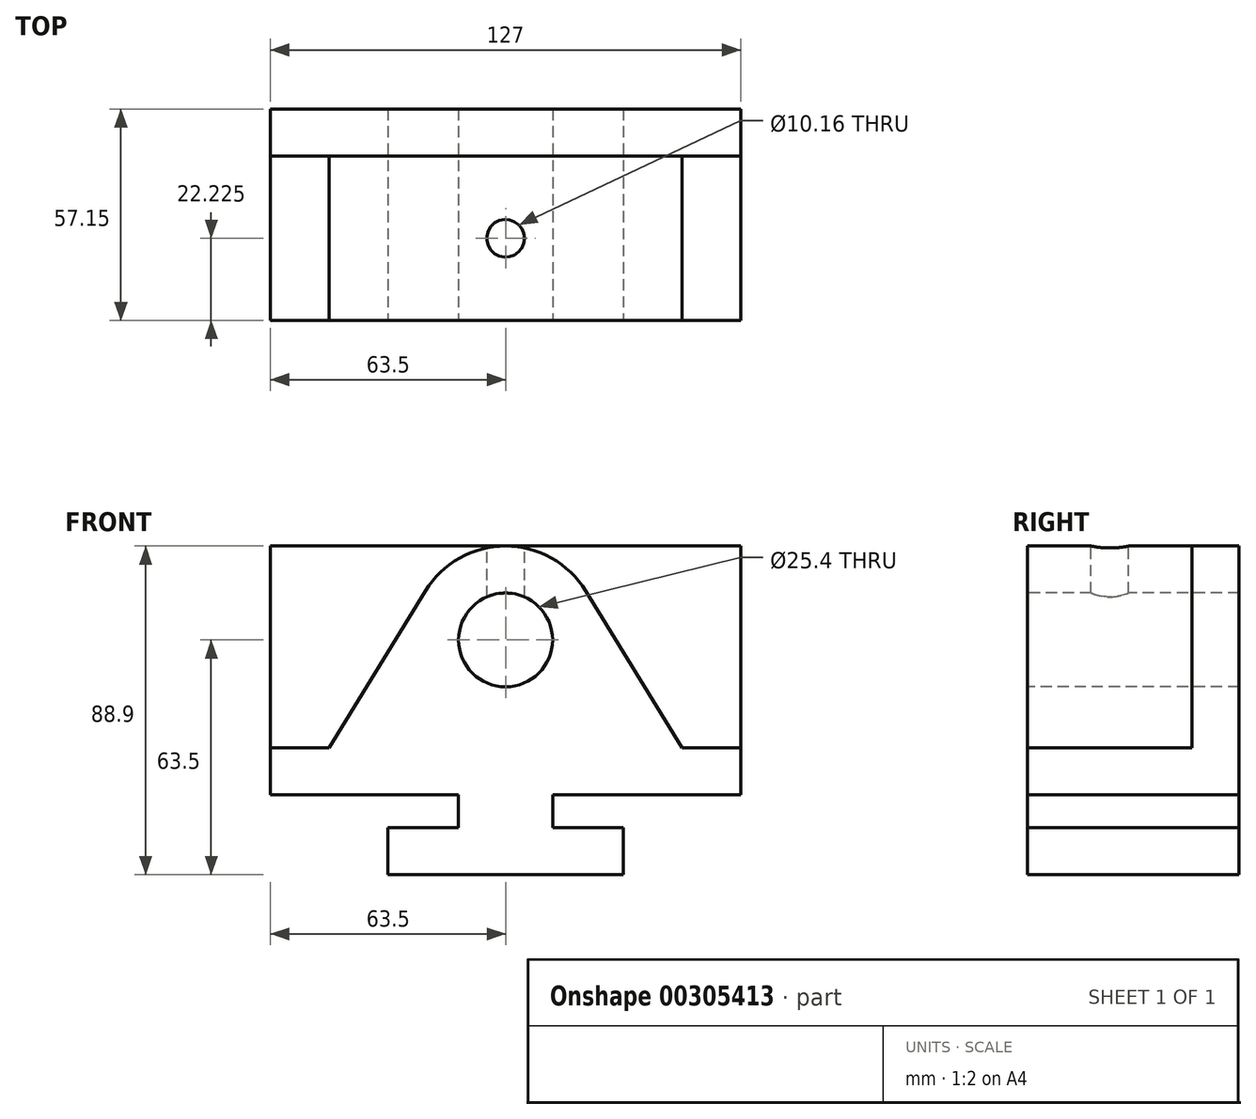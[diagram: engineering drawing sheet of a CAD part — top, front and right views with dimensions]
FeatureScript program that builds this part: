
annotation { "Feature Type Name" : "Feature", "Feature Type Description" : "" }
export const myFeature = defineFeature(function(context is Context, id is Id, definition is map)
    precondition{}
    {
        {
            var Q0;
            Q0=qCreatedBy(makeId("Front.planeOp"),FACE);
            var sketch = newSketch(context, id + "F0", { "sketchPlane" : qUnion([Q0])});
            skLineSegment(sketch, "E0.bottom", {"start": v(0, 0) * mm, "end": v(127, 0) * mm});
            skLineSegment(sketch, "E0.top", {"start": v(0, 88.9) * mm, "end": v(127, 88.9) * mm});
            skLineSegment(sketch, "E0.left", {"start": v(0, 0) * mm, "end": v(0, 88.9) * mm});
            skLineSegment(sketch, "E0.right", {"start": v(127, 0) * mm, "end": v(127, 88.9) * mm});
            skSolve(sketch);
        }
        {
            var Q0;
            Q0 = qSketchRegion(id + "F0", true);
            extrude(context, id + "F1", {"entities" : qUnion([Q0]), "depth" : 57.15 * mm});
        }
        {
            var Q0;
            Q0=makeQuery(id+"F1.opExtrude","CAP_FACE",FACE,{"disambiguationData":[OSD([sQuery(id+"F0.wireOp",EDGE,"E0.bottom"),sQuery(id+"F0.wireOp",EDGE,"E0.top"),sQuery(id+"F0.wireOp",EDGE,"E0.left"),sQuery(id+"F0.wireOp",EDGE,"E0.right")])],"isStart":false});
            var sketch = newSketch(context, id + "F2", { "sketchPlane" : qUnion([Q0])});
            skCircle(sketch, "E1", {"center": v(63.5, 63.5) * mm, "radius": 12.7 * mm});
            skArc(sketch, "E2", {"start": v(85.17, 76.75) * mm, "mid": v(63.5, 88.9) * mm, "end": v(41.83, 76.75) * mm});
            skLineSegment(sketch, "E3", {"start": v(0, 34.3) * mm, "end": v(15.88, 34.3) * mm});
            skLineSegment(sketch, "E4", {"start": v(15.88, 34.3) * mm, "end": v(41.83, 76.75) * mm});
            skLineSegment(sketch, "E5", {"start": v(127, 34.3) * mm, "end": v(111.12, 34.3) * mm});
            skLineSegment(sketch, "E6", {"start": v(111.12, 34.3) * mm, "end": v(85.17, 76.75) * mm});
            skLineSegment(sketch, "E7", {"start": v(0, 21.59) * mm, "end": v(50.8, 21.59) * mm});
            skLineSegment(sketch, "E8", {"start": v(50.8, 21.59) * mm, "end": v(50.8, 12.7) * mm});
            skLineSegment(sketch, "E9", {"start": v(76.2, 21.6) * mm, "end": v(76.2, 12.7) * mm});
            skLineSegment(sketch, "E10.trimOffspring", {"start": v(76.2, 21.59) * mm, "end": v(127, 21.59) * mm});
            skLineSegment(sketch, "E11", {"start": v(76.2, 12.7) * mm, "end": v(95.25, 12.7) * mm});
            skLineSegment(sketch, "E12", {"start": v(50.8, 12.7) * mm, "end": v(31.75, 12.7) * mm});
            skLineSegment(sketch, "E13", {"start": v(31.75, 12.7) * mm, "end": v(31.75, 0) * mm});
            skLineSegment(sketch, "E14", {"start": v(31.75, 0) * mm, "end": v(95.25, 0) * mm});
            skLineSegment(sketch, "E15", {"start": v(95.25, 0) * mm, "end": v(95.25, 12.7) * mm});
            skSolve(sketch);
        }
        {
            var Q0;
            Q0 = qSketchRegion(id + "F2", true);
            var Q1;
            Q1=makeQuery(id+"F2.imprint","IMPRINT",FACE,{"disambiguationData":[TD([[makeQuery(id+"F2.imprint","IMPRINT",EDGE,{"derivedFrom":sQuery(id+"F2.wireOp",EDGE,"E9")}),1.0]])]});
            var Q2;
            {var subQ1=sQuery(id+"F2.wireOp",EDGE,"E7");Q2=makeQuery(id+"F2.imprint","IMPRINT",FACE,{"disambiguationData":[TD([[makeQuery(id+"F2.imprint","IMPRINT",EDGE,{"derivedFrom":subQ1}),-1.0]])]});}
            extrude(context, id + "F3", {"entities" : qUnion([Q0, Q1, Q2]), "operationType" : NewBodyOperationType.REMOVE, "endBound" : BoundingType.THROUGH_ALL, "oppositeDirection" : true, "depth" : 25.4 * mm});
        }
        {
            var Q0;
            Q0=makeQuery(id+"F1.opExtrude","CAP_FACE",FACE,{"disambiguationData":[OSD([sQuery(id+"F0.wireOp",EDGE,"E0.bottom"),sQuery(id+"F0.wireOp",EDGE,"E0.top"),sQuery(id+"F0.wireOp",EDGE,"E0.left"),sQuery(id+"F0.wireOp",EDGE,"E0.right")])],"isStart":false});
            var sketch = newSketch(context, id + "F4", { "sketchPlane" : qUnion([Q0])});
            skCircle(sketch, "E16", {"center": v(63.5, 63.5) * mm, "radius": 25.4 * mm});
            skLineSegment(sketch, "E17", {"start": v(0, 34.3) * mm, "end": v(15.88, 34.3) * mm});
            skLineSegment(sketch, "E18", {"start": v(127, 34.3) * mm, "end": v(111.12, 34.3) * mm});
            skLineSegment(sketch, "E19", {"start": v(15.88, 34.3) * mm, "end": v(41.83, 76.75) * mm});
            skLineSegment(sketch, "E20", {"start": v(111.12, 34.3) * mm, "end": v(85.17, 76.75) * mm});
            skSolve(sketch);
        }
        {
            var Q0;
            {var subQ6=sQuery(id+"F4.wireOp",EDGE,"E17");Q0=makeQuery(id+"F4.imprint","IMPRINT",FACE,{"disambiguationData":[TD([[makeQuery(id+"F4.imprint","IMPRINT",EDGE,{"derivedFrom":subQ6}),1.0]])]});}
            var Q1;
            {var subQ6=sQuery(id+"F4.wireOp",EDGE,"E18");Q1=makeQuery(id+"F4.imprint","IMPRINT",FACE,{"disambiguationData":[TD([[makeQuery(id+"F4.imprint","IMPRINT",EDGE,{"derivedFrom":subQ6}),-1.0]])]});}
            extrude(context, id + "F5", {"entities" : qUnion([Q0, Q1]), "operationType" : NewBodyOperationType.REMOVE, "oppositeDirection" : true, "depth" : 44.45 * mm});
        }
        {
            var Q0;
            Q0=makeQuery(id+"F1.opExtrude","SWEPT_FACE",FACE,{"disambiguationData":[OSD([sQuery(id+"F0.wireOp",EDGE,"E0.top")])]});
            var sketch = newSketch(context, id + "F6", { "sketchPlane" : qUnion([Q0])});
            skCircle(sketch, "E21", {"center": v(63.5, -34.93) * mm, "radius": 5.08 * mm});
            skSolve(sketch);
        }
        {
            var Q0;
            Q0 = qSketchRegion(id + "F6", true);
            extrude(context, id + "F7", {"entities" : qUnion([Q0]), "operationType" : NewBodyOperationType.REMOVE, "oppositeDirection" : true, "depth" : 25.4 * mm});
        }
    });
